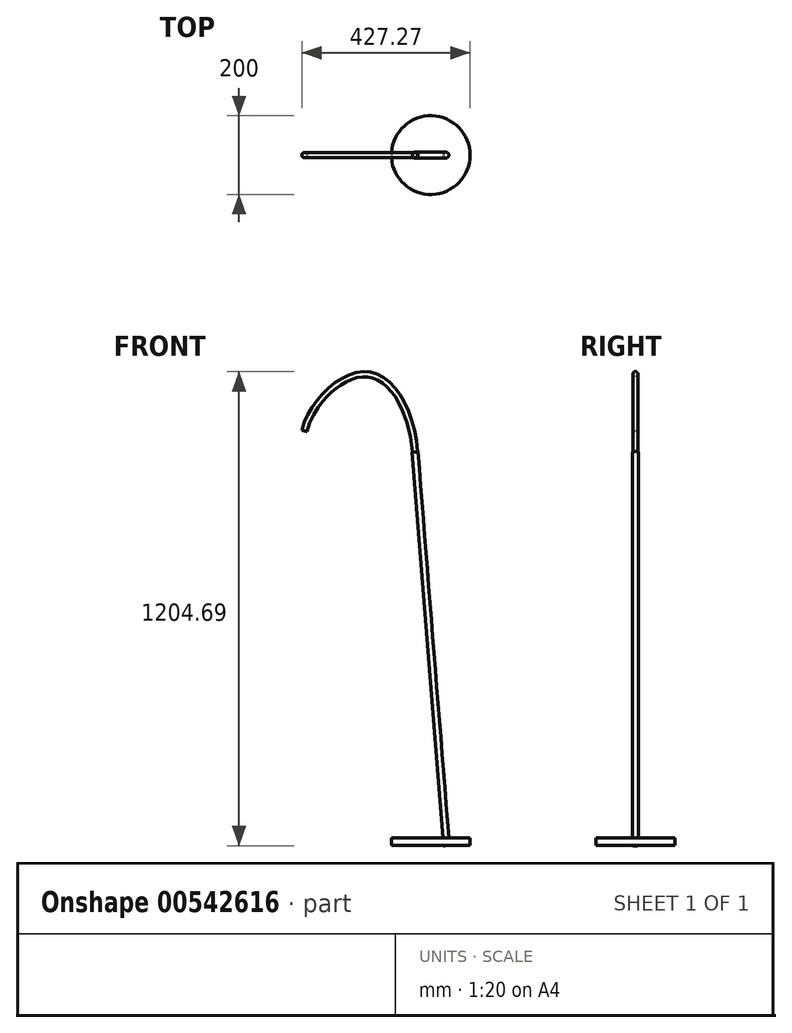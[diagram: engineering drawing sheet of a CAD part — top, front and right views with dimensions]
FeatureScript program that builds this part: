
annotation { "Feature Type Name" : "Feature", "Feature Type Description" : "" }
export const myFeature = defineFeature(function(context is Context, id is Id, definition is map)
    precondition{}
    {
        {
            var Q0;
            Q0=qCreatedBy(makeId("Top.planeOp"),FACE);
            var sketch = newSketch(context, id + "F0", { "sketchPlane" : qUnion([Q0])});
            skCircle(sketch, "E0", {"center": v(0, 0) * mm, "radius": 100 * mm});
            skSolve(sketch);
        }
        {
            var Q0;
            Q0=makeQuery(id+"F0.imprint","IMPRINT",FACE,{"disambiguationData":[TD([[makeQuery(id+"F0.imprint","IMPRINT",EDGE,{"derivedFrom":sQuery(id+"F0.wireOp",EDGE,"E0")}),1.0]])]});
            extrude(context, id + "F1", {"entities" : qUnion([Q0]), "depth" : 20 * mm, "offsetDistance" : 25 * mm});
        }
        {
            var Q0;
            Q0=qCreatedBy(makeId("Front.planeOp"),FACE);
            var sketch = newSketch(context, id + "F2", { "sketchPlane" : qUnion([Q0])});
            skLineSegment(sketch, "E1", {"start": v(0, 0) * mm, "end": v(0, 1000) * mm, "construction": true});
            skLineSegment(sketch, "E2", {"start": v(0, 1000) * mm, "end": v(-40, 1000) * mm, "construction": true});
            skLineSegment(sketch, "E3", {"start": v(-40, 1000) * mm, "end": v(40, 0) * mm, "construction": true});
            skLineSegment(sketch, "E4", {"start": v(40, 0) * mm, "end": v(0, 0) * mm, "construction": true});
            skLineSegment(sketch, "E5", {"start": v(-33.52, 1000.52) * mm, "end": v(46.48, 0.52) * mm});
            skLineSegment(sketch, "E6", {"start": v(46.48, 0.52) * mm, "end": v(47.48, 0.6) * mm});
            skLineSegment(sketch, "E7", {"start": v(47.48, 0.6) * mm, "end": v(-32.52, 1000.6) * mm});
            skLineSegment(sketch, "E8", {"start": v(-32.52, 1000.6) * mm, "end": v(-33.52, 1000.52) * mm});
            skPoint(sketch, "E9", {"position": v(-32.52, 1000.13) * mm});
            skFitSpline(sketch, "E10", {"points": [v(-40, 1000) * mm, v(-167.88, 1197.59) * mm, v(-320.95, 1053.36) * mm], "startDerivative": vector(-51.96, 649.5) * mm, "endDerivative": vector(-101.8, -426.66) * mm});
            skSolve(sketch);
        }
        {
            var Q0;
            Q0=makeQuery(id+"F2.imprint","IMPRINT",FACE,{"disambiguationData":[TD([[makeQuery(id+"F2.imprint","IMPRINT",EDGE,{"derivedFrom":sQuery(id+"F2.wireOp",EDGE,"E5")}),1.0]])]});
            var Q1;
            Q1=sQuery(id+"F2.wireOp",EDGE,"E3");
            revolve(context, id + "F3", {"operationType" : NewBodyOperationType.ADD, "entities" : qUnion([Q0]), "axis" : qUnion([Q1]), "revolveType" : RevolveType.FULL});
        }
        {
            var Q0;
            Q0=makeQuery(id+"F3.opRevolve","SWEPT_FACE",FACE,{"disambiguationData":[OSD([sQuery(id+"F2.wireOp",EDGE,"E8")])]});
            var sketch = newSketch(context, id + "F4", { "sketchPlane" : qUnion([Q0])});
            skCircle(sketch, "E11.0", {"center": v(39.87, 0) * mm, "radius": 6.5 * mm});
            skSolve(sketch);
        }
        {
            var Q0;
            Q0=makeQuery(id+"F4.imprint","IMPRINT",FACE,{"disambiguationData":[TD([[makeQuery(id+"F4.imprint","IMPRINT",EDGE,{"derivedFrom":sQuery(id+"F4.wireOp",EDGE,"E11.0")}),1.0]])]});
            var Q1;
            Q1=sQuery(id+"F2.wireOp",EDGE,"E10");
            sweep(context, id + "F5", {"profiles" : qUnion([Q0]), "path" : qUnion([Q1])});
        }
    });
